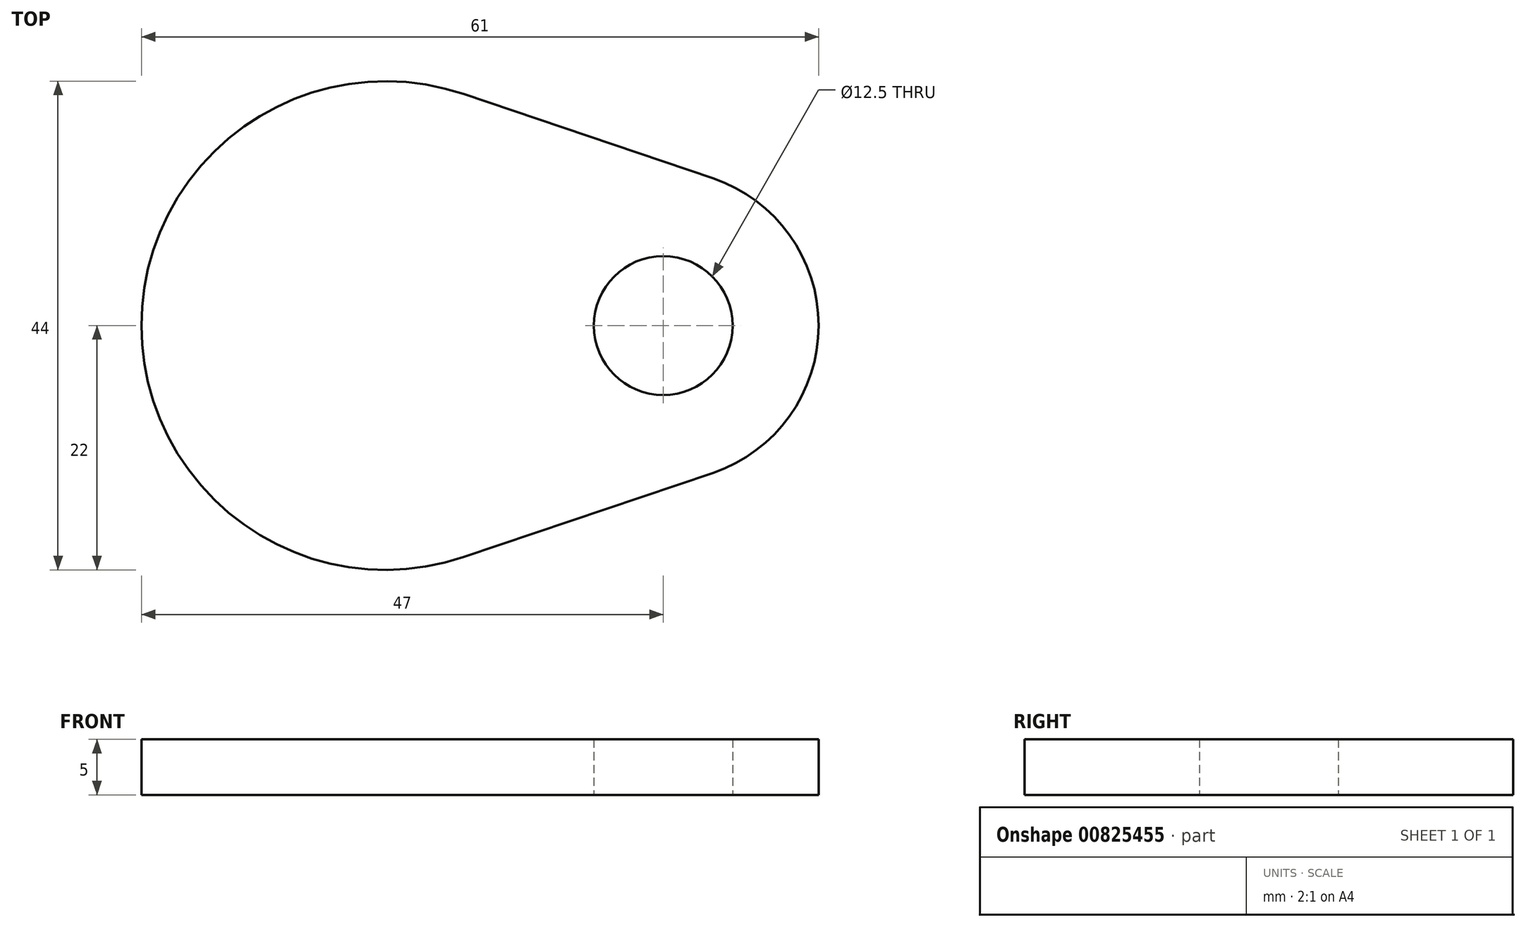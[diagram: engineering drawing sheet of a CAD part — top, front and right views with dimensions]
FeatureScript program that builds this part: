
annotation { "Feature Type Name" : "Feature", "Feature Type Description" : "" }
export const myFeature = defineFeature(function(context is Context, id is Id, definition is map)
    precondition{}
    {
        {
            var Q0;
            Q0=qCreatedBy(makeId("Top.planeOp"),FACE);
            var sketch = newSketch(context, id + "F0", { "sketchPlane" : qUnion([Q0])});
            skCircle(sketch, "E0", {"center": v(0, 0) * mm, "radius": 14 * mm});
            skCircle(sketch, "E1", {"center": v(-25, 0) * mm, "radius": 22 * mm});
            skLineSegment(sketch, "E2", {"start": v(-17.96, 20.84) * mm, "end": v(4.48, 13.26) * mm});
            skLineSegment(sketch, "E3", {"start": v(4.48, -13.26) * mm, "end": v(-17.96, -20.84) * mm});
            skCircle(sketch, "E4", {"center": v(0, 0) * mm, "radius": 6.25 * mm});
            skSolve(sketch);
        }
        {
            var Q0;
            {var subQ0=sQuery(id+"F0.wireOp",EDGE,"E1");var subQ1=sQuery(id+"F0.wireOp",EDGE,"E0");var subQ2=makeQuery(id+"F0.imprint","INTERSECT",VERTEX,{"disambiguationData":[OD(0.0)],"derivedFrom":[subQ1,subQ0]});Q0=makeQuery(id+"F0.imprint","IMPRINT",FACE,{"disambiguationData":[TD([[makeQuery(id+"F0.imprint","IMPRINT",EDGE,{"disambiguationData":[TD([[subQ2,-1.0]])],"derivedFrom":subQ1}),-1.0]])]});}
            var Q1;
            {var subQ0=sQuery(id+"F0.wireOp",EDGE,"E2");Q1=makeQuery(id+"F0.imprint","IMPRINT",FACE,{"disambiguationData":[TD([[makeQuery(id+"F0.imprint","IMPRINT",EDGE,{"derivedFrom":subQ0}),-1.0]])]});}
            var Q2;
            {var subQ0=sQuery(id+"F0.wireOp",EDGE,"E1");var subQ1=sQuery(id+"F0.wireOp",EDGE,"E0");var subQ2=makeQuery(id+"F0.imprint","INTERSECT",VERTEX,{"disambiguationData":[OD(0.0)],"derivedFrom":[subQ1,subQ0]});Q2=makeQuery(id+"F0.imprint","IMPRINT",FACE,{"disambiguationData":[TD([[makeQuery(id+"F0.imprint","IMPRINT",EDGE,{"disambiguationData":[TD([[subQ2,-1.0]])],"derivedFrom":subQ1}),1.0]])]});}
            var Q3;
            {var subQ0=sQuery(id+"F0.wireOp",EDGE,"E0");var subQ1=makeQuery(id+"F0.imprint","INTERSECT",VERTEX,{"derivedFrom":[subQ0,sQuery(id+"F0.wireOp",EDGE,"E2")]});Q3=makeQuery(id+"F0.imprint","IMPRINT",FACE,{"disambiguationData":[TD([[makeQuery(id+"F0.imprint","IMPRINT",EDGE,{"disambiguationData":[TD([[subQ1,-1.0]])],"derivedFrom":subQ0}),1.0]])]});}
            var Q4;
            {var subQ0=sQuery(id+"F0.wireOp",EDGE,"E3");Q4=makeQuery(id+"F0.imprint","IMPRINT",FACE,{"disambiguationData":[TD([[makeQuery(id+"F0.imprint","IMPRINT",EDGE,{"derivedFrom":subQ0}),-1.0]])]});}
            extrude(context, id + "F1", {"entities" : qUnion([Q0, Q1, Q2, Q3, Q4]), "depth" : 5 * mm, "offsetDistance" : 25 * mm});
        }
    });
